# Revit family: Beam-Wood-Allweather_Wood
name_source: partatom
category: Structural Framing
units: mm (PartAtom-declared; Revit-internal decimal feet)

## family parameters
Always export as geometry = No
Always vertical = Yes
Classification Number = 23.25.30.11.14.14
Cut with Voids When Loaded = No
Material for Model Behavior = Wood
Section Shape = Not Defined
Shared = No
Show family pre-cut in plan views = Yes
Structural Framing Length Roundoff = 0' - 0"

## types (7) — shared parameters
Assembly Code = B10
Description = Wood Beam
Finish Characteristic = S4S Lumber
Keynote = 06 05 73
Manufacturer = Allweather Wood
Moisture Content (Green or Dry) = Dry
Preservative = Fire Retardant
Specifications = https://www.arcat.com
Structural Material = Lumber - Allweather Wood
URL = https://www.arcat.com
Wood Species = Douglas-fir / Mixed Species

## per-type parameters (varying)
| type | Actual Size | Model | Nominal Size | b | d |
| Fire Retardant S4S Lumber - 2 x 4 | 1-1/2x3-1/2 inches | 2" x 4" | 2" x 4" | 0' - 1 1/2" | 0' - 3 1/2" |
| Fire Retardant S4S Lumber - 6 x 6 | 5-1/2x5-1/2 inches | 6" x 6" | 6" x 6" | 0' - 5 1/2" | 0' - 5 1/2" |
| Fire Retardant S4S Lumber - 2 x 12 | 1-1/2x10-1/4 inches | 2" x 12" | 2" x 12" | 0' - 1 1/2" | 0' - 10 1/4" |
| Fire Retardant S4S Lumber - 4 x 6 | 3-9/16 x 5-5/8  inches | 4" x 6" | 4" x 6" | 0' - 3 9/16" | 0' - 5 5/8" |
| Fire Retardant S4S Lumber - 2 x 10 | 1-1/2x9-1/4 inches | 2" x 10" | 2" x 10" | 0' - 1 1/2" | 0' - 9 1/4" |
| Fire Retardant S4S Lumber - 2 x 8 | 1-1/2x7-1/4 inches | 2" x 8" | 2" x 8" | 0' - 1 1/2" | 0' - 7 1/4" |
| Fire Retardant S4S Lumber - 2 x 6 | 1-1/2x5-1/2 inches | 2" x 6" | 2" x 6" | 0' - 1 1/2" | 0' - 5 1/2" |

## geometry (parser evidence)
native form markers: Sweep x1
no freeform markers — native parametric forms only
